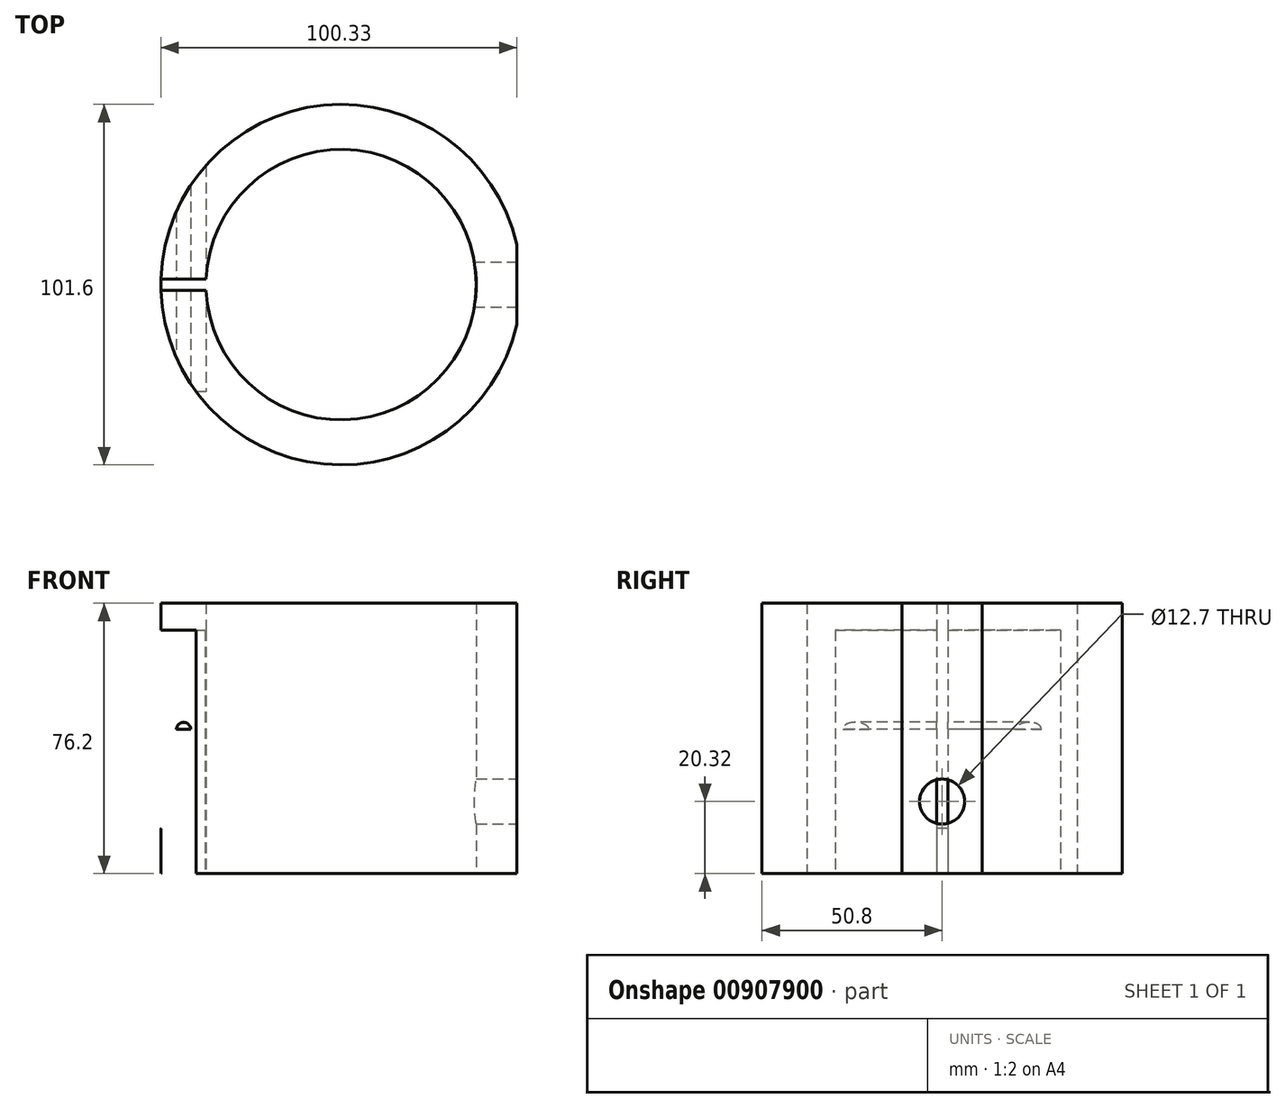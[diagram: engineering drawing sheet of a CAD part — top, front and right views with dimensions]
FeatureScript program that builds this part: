
annotation { "Feature Type Name" : "Feature", "Feature Type Description" : "" }
export const myFeature = defineFeature(function(context is Context, id is Id, definition is map)
    precondition{}
    {
        {
            var Q0;
            Q0=qCreatedBy(makeId("Top.planeOp"),FACE);
            var sketch = newSketch(context, id + "F0", { "sketchPlane" : qUnion([Q0])});
            skCircle(sketch, "E0", {"center": v(0, 0) * mm, "radius": 38.1 * mm});
            skCircle(sketch, "E1", {"center": v(0, 0) * mm, "radius": 50.8 * mm});
            skCircle(sketch, "E2", {"center": v(0, 0) * mm, "radius": 6.35 * mm});
            skLineSegment(sketch, "E3", {"start": v(-38.07, -1.59) * mm, "end": v(-50.78, -1.59) * mm});
            skLineSegment(sketch, "E4", {"start": v(-38.07, 1.59) * mm, "end": v(-50.78, 1.59) * mm});
            skPoint(sketch, "E5.start.orphan", {"position": v(-38.1, 0) * mm});
            skSolve(sketch);
        }
        {
            var Q0;
            Q0=makeQuery(id+"F0.imprint","IMPRINT",FACE,{"disambiguationData":[TD([[makeQuery(id+"F0.imprint","IMPRINT",EDGE,{"derivedFrom":sQuery(id+"F0.wireOp",EDGE,"E0")}),1.0]])]});
            var sketch = newSketch(context, id + "F1", { "sketchPlane" : qUnion([Q0])});
            skSolve(sketch);
        }
        {
            var Q0;
            Q0=makeQuery(id+"F1.imprint","IMPRINT",FACE,{"disambiguationData":[TD([[makeQuery(id+"F1.imprint","IMPRINT",EDGE,{"derivedFrom":makeQuery(id+"F0.imprint","IMPRINT",EDGE,{"derivedFrom":sQuery(id+"F0.wireOp",EDGE,"E2")})}),-1.0]])]});
            var Q1;
            {var subQ0=sQuery(id+"F0.wireOp",EDGE,"E3");Q1=makeQuery(id+"F0.imprint","IMPRINT",FACE,{"disambiguationData":[TD([[makeQuery(id+"F0.imprint","IMPRINT",EDGE,{"derivedFrom":subQ0}),-1.0]])]});}
            extrude(context, id + "F2", {"entities" : qUnion([Q0, Q1]), "depth" : 12.7 * mm, "offsetDistance" : 25.4 * mm});
        }
        {
            var Q0;
            {var subQ0=sQuery(id+"F0.wireOp",EDGE,"E3");Q0=makeQuery(id+"F0.imprint","IMPRINT",FACE,{"disambiguationData":[TD([[makeQuery(id+"F0.imprint","IMPRINT",EDGE,{"derivedFrom":subQ0}),1.0]])]});}
            extrude(context, id + "F3", {"entities" : qUnion([Q0]), "depth" : 76.2 * mm, "offsetDistance" : 25.4 * mm});
        }
        {
            var Q0;
            Q0=makeQuery(id+"F3.opExtrude","SWEPT_FACE",FACE,{"disambiguationData":[OSD([sQuery(id+"F0.wireOp",EDGE,"E4")])]});
            var sketch = newSketch(context, id + "F4", { "sketchPlane" : qUnion([Q0])});
            skLineSegment(sketch, "E6", {"start": v(-44.42, 76.2) * mm, "end": v(-44.42, 0) * mm});
            skLineSegment(sketch, "E7", {"start": v(-50.78, 68.58) * mm, "end": v(-38.07, 68.58) * mm});
            skLineSegment(sketch, "E8", {"start": v(-50.78, 40.64) * mm, "end": v(-38.07, 40.64) * mm});
            skCircle(sketch, "E9", {"center": v(-44.42, 68.58) * mm, "radius": 2.02 * mm});
            skCircle(sketch, "E10", {"center": v(-44.42, 40.64) * mm, "radius": 2.02 * mm});
            skSolve(sketch);
        }
        {
            var Q0;
            {var subQ0=sQuery(id+"F4.wireOp",EDGE,"E9");var subQ1=sQuery(id+"F4.wireOp",EDGE,"E6");var subQ2=makeQuery(id+"F4.imprint","INTERSECT",VERTEX,{"disambiguationData":[OD(0.0)],"derivedFrom":[subQ1,subQ0]});Q0=makeQuery(id+"F4.imprint","IMPRINT",FACE,{"disambiguationData":[TD([[makeQuery(id+"F4.imprint","IMPRINT",EDGE,{"disambiguationData":[TD([[subQ2,-1.0]])],"derivedFrom":subQ1}),1.0]])]});}
            var Q1;
            {var subQ0=sQuery(id+"F4.wireOp",EDGE,"E9");var subQ1=sQuery(id+"F4.wireOp",EDGE,"E6");var subQ2=makeQuery(id+"F4.imprint","INTERSECT",VERTEX,{"disambiguationData":[OD(0.0)],"derivedFrom":[subQ1,subQ0]});Q1=makeQuery(id+"F4.imprint","IMPRINT",FACE,{"disambiguationData":[TD([[makeQuery(id+"F4.imprint","IMPRINT",EDGE,{"disambiguationData":[TD([[subQ2,-1.0]])],"derivedFrom":subQ1}),-1.0]])]});}
            var Q2;
            {var subQ0=sQuery(id+"F4.wireOp",EDGE,"E7");var subQ1=sQuery(id+"F4.wireOp",EDGE,"E6");var subQ2=makeQuery(id+"F4.imprint","INTERSECT",VERTEX,{"derivedFrom":[subQ1,subQ0]});Q2=makeQuery(id+"F4.imprint","IMPRINT",FACE,{"disambiguationData":[TD([[makeQuery(id+"F4.imprint","IMPRINT",EDGE,{"disambiguationData":[TD([[subQ2,-1.0]])],"derivedFrom":subQ1}),-1.0]])]});}
            var Q3;
            {var subQ0=sQuery(id+"F4.wireOp",EDGE,"E7");var subQ1=sQuery(id+"F4.wireOp",EDGE,"E6");var subQ2=makeQuery(id+"F4.imprint","INTERSECT",VERTEX,{"derivedFrom":[subQ1,subQ0]});Q3=makeQuery(id+"F4.imprint","IMPRINT",FACE,{"disambiguationData":[TD([[makeQuery(id+"F4.imprint","IMPRINT",EDGE,{"disambiguationData":[TD([[subQ2,-1.0]])],"derivedFrom":subQ1}),1.0]])]});}
            var Q4;
            {var subQ0=sQuery(id+"F4.wireOp",EDGE,"E10");var subQ1=sQuery(id+"F4.wireOp",EDGE,"E6");var subQ2=makeQuery(id+"F4.imprint","INTERSECT",VERTEX,{"disambiguationData":[OD(0.0)],"derivedFrom":[subQ1,subQ0]});Q4=makeQuery(id+"F4.imprint","IMPRINT",FACE,{"disambiguationData":[TD([[makeQuery(id+"F4.imprint","IMPRINT",EDGE,{"disambiguationData":[TD([[subQ2,-1.0]])],"derivedFrom":subQ1}),-1.0]])]});}
            var Q5;
            {var subQ0=sQuery(id+"F4.wireOp",EDGE,"E10");var subQ1=sQuery(id+"F4.wireOp",EDGE,"E6");var subQ2=makeQuery(id+"F4.imprint","INTERSECT",VERTEX,{"disambiguationData":[OD(0.0)],"derivedFrom":[subQ1,subQ0]});Q5=makeQuery(id+"F4.imprint","IMPRINT",FACE,{"disambiguationData":[TD([[makeQuery(id+"F4.imprint","IMPRINT",EDGE,{"disambiguationData":[TD([[subQ2,-1.0]])],"derivedFrom":subQ1}),1.0]])]});}
            var Q6;
            {var subQ0=sQuery(id+"F4.wireOp",EDGE,"E8");var subQ1=sQuery(id+"F4.wireOp",EDGE,"E6");var subQ2=makeQuery(id+"F4.imprint","INTERSECT",VERTEX,{"derivedFrom":[subQ1,subQ0]});Q6=makeQuery(id+"F4.imprint","IMPRINT",FACE,{"disambiguationData":[TD([[makeQuery(id+"F4.imprint","IMPRINT",EDGE,{"disambiguationData":[TD([[subQ2,-1.0]])],"derivedFrom":subQ1}),1.0]])]});}
            var Q7;
            {var subQ0=sQuery(id+"F4.wireOp",EDGE,"E8");var subQ1=sQuery(id+"F4.wireOp",EDGE,"E6");var subQ2=makeQuery(id+"F4.imprint","INTERSECT",VERTEX,{"derivedFrom":[subQ1,subQ0]});Q7=makeQuery(id+"F4.imprint","IMPRINT",FACE,{"disambiguationData":[TD([[makeQuery(id+"F4.imprint","IMPRINT",EDGE,{"disambiguationData":[TD([[subQ2,-1.0]])],"derivedFrom":subQ1}),-1.0]])]});}
            var Q8;
            Q8=sQuery(id+"F4.wireOp",EDGE,"E9");
            var Q9;
            Q9=sQuery(id+"F4.wireOp",EDGE,"E10");
            extrude(context, id + "F5", {"entities" : qUnion([Q0, Q1, Q2, Q3, Q4, Q5, Q6, Q7]), "operationType" : NewBodyOperationType.REMOVE, "surfaceEntities" : qUnion([Q8, Q9]), "oppositeDirection" : true, "depth" : 31.75 * mm, "offsetDistance" : 25.4 * mm, "hasSecondDirection" : true, "secondDirectionOppositeDirection" : false, "secondDirectionDepth" : 31.75 * mm});
        }
        {
            var Q0;
            Q0=makeQuery(id+"F3.opExtrude","CAP_FACE",FACE,{"disambiguationData":[OSD([sQuery(id+"F0.wireOp",EDGE,"E0"),sQuery(id+"F0.wireOp",EDGE,"E1"),sQuery(id+"F0.wireOp",EDGE,"E3"),sQuery(id+"F0.wireOp",EDGE,"E4")])],"isStart":false});
            var sketch = newSketch(context, id + "F6", { "sketchPlane" : qUnion([Q0])});
            skLineSegment(sketch, "E11", {"start": v(50.8, 0) * mm, "end": v(38.1, 0) * mm});
            skLineSegment(sketch, "E12", {"start": v(49.53, 0) * mm, "end": v(49.53, -11.29) * mm});
            skLineSegment(sketch, "E13", {"start": v(49.53, 0) * mm, "end": v(49.53, 11.29) * mm});
            skSolve(sketch);
        }
        {
            var Q0;
            Q0 = qSketchRegion(id + "F6", true);
            var Q1;
            {var subQ3=sQuery(id+"F6.wireOp",EDGE,"E12");Q1=makeQuery(id+"F6.imprint","IMPRINT",FACE,{"disambiguationData":[TD([[makeQuery(id+"F6.imprint","IMPRINT",EDGE,{"derivedFrom":subQ3}),1.0]])]});}
            var Q2;
            {var subQ3=sQuery(id+"F6.wireOp",EDGE,"E13");Q2=makeQuery(id+"F6.imprint","IMPRINT",FACE,{"disambiguationData":[TD([[makeQuery(id+"F6.imprint","IMPRINT",EDGE,{"derivedFrom":subQ3}),-1.0]])]});}
            extrude(context, id + "F7", {"entities" : qUnion([Q0, Q1, Q2]), "operationType" : NewBodyOperationType.REMOVE, "oppositeDirection" : true, "depth" : 76.2 * mm, "offsetDistance" : 25.4 * mm});
        }
        {
            var Q0;
            Q0=makeQuery(id+"F7.boolean.opBoolean","COPY",FACE,{"derivedFrom":makeQuery(id+"F7.opExtrude","SWEPT_FACE",FACE,{"disambiguationData":[OSD([sQuery(id+"F6.wireOp",EDGE,"E12"),sQuery(id+"F6.wireOp",EDGE,"E13")])]})});
            var sketch = newSketch(context, id + "F8", { "sketchPlane" : qUnion([Q0])});
            skLineSegment(sketch, "E14", {"start": v(0, 0) * mm, "end": v(0, 76.2) * mm, "construction": true});
            skLineSegment(sketch, "E15", {"start": v(-11.29, 20.32) * mm, "end": v(11.29, 20.32) * mm, "construction": true});
            skCircle(sketch, "E16", {"center": v(0, 20.32) * mm, "radius": 6.35 * mm});
            skSolve(sketch);
        }
        {
            var Q0;
            Q0=makeQuery(id+"F8.imprint","IMPRINT",FACE,{"disambiguationData":[TD([[makeQuery(id+"F8.imprint","IMPRINT",EDGE,{"derivedFrom":sQuery(id+"F8.wireOp",EDGE,"E16")}),1.0]])]});
            var Q1;
            Q1=sQuery(id+"F8.wireOp",EDGE,"E16");
            extrude(context, id + "F9", {"entities" : qUnion([Q0]), "operationType" : NewBodyOperationType.REMOVE, "surfaceEntities" : qUnion([Q1]), "oppositeDirection" : true, "depth" : 12.7 * mm, "offsetDistance" : 25.4 * mm});
        }
    });
